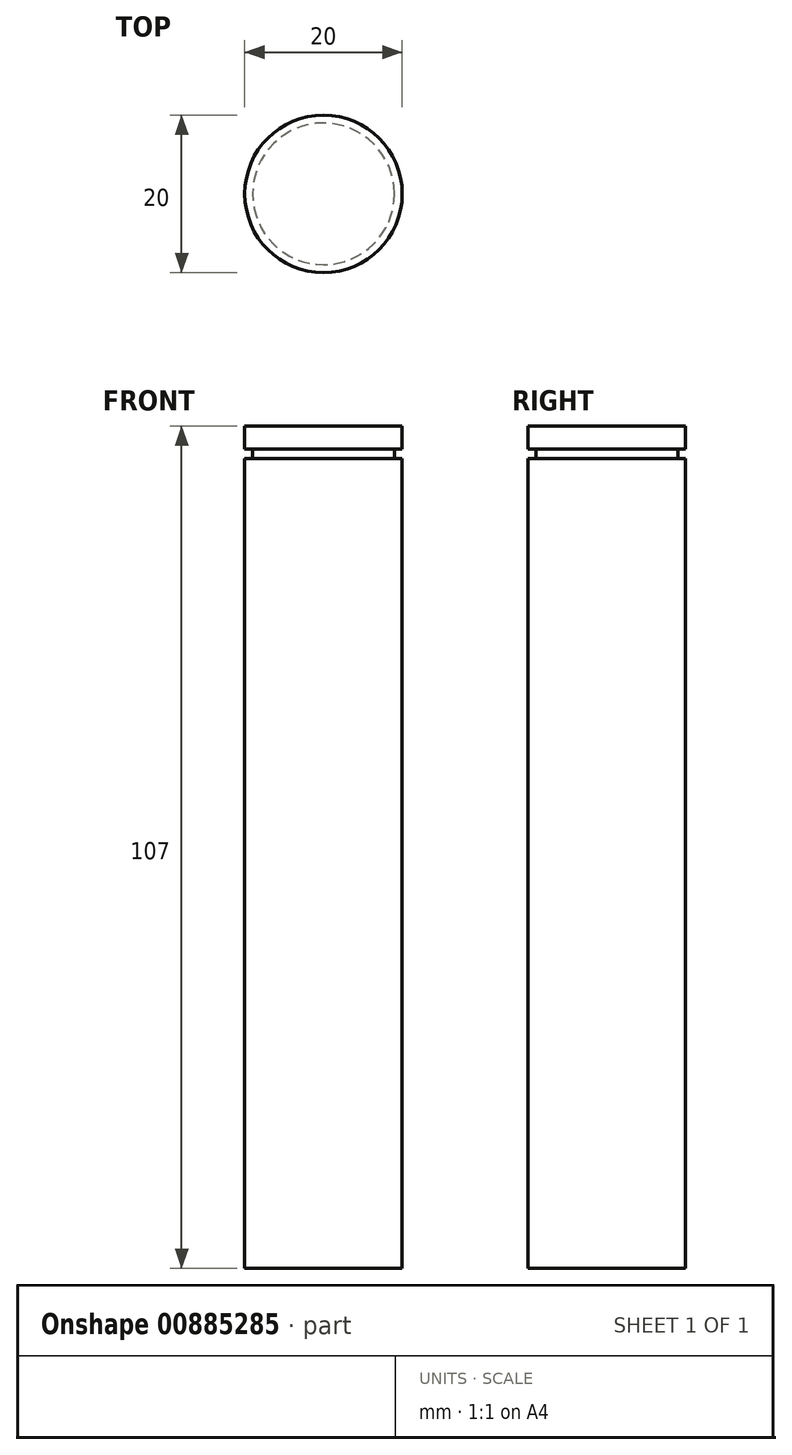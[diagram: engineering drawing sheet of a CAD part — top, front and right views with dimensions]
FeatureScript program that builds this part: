
annotation { "Feature Type Name" : "Feature", "Feature Type Description" : "" }
export const myFeature = defineFeature(function(context is Context, id is Id, definition is map)
    precondition{}
    {
        {
            var Q0;
            Q0=qCreatedBy(makeId("Front.planeOp"),FACE);
            var sketch = newSketch(context, id + "F0", { "sketchPlane" : qUnion([Q0])});
            skLineSegment(sketch, "E0.bottom", {"start": v(0, 0) * mm, "end": v(-20, 0) * mm});
            skLineSegment(sketch, "E0.top", {"start": v(0, 107) * mm, "end": v(-20, 107) * mm});
            skLineSegment(sketch, "E0.left", {"start": v(0, 0) * mm, "end": v(0, 107) * mm});
            skLineSegment(sketch, "E0.right", {"start": v(-20, 0) * mm, "end": v(-20, 107) * mm});
            skLineSegment(sketch, "E1", {"start": v(-10, 107) * mm, "end": v(-10, 0) * mm});
            skLineSegment(sketch, "E2.bottom", {"start": v(-20, 104.1) * mm, "end": v(-19, 104.1) * mm});
            skLineSegment(sketch, "E2.top", {"start": v(-20, 102.85) * mm, "end": v(-19, 102.85) * mm});
            skLineSegment(sketch, "E2.left", {"start": v(-20, 104.1) * mm, "end": v(-20, 102.85) * mm});
            skLineSegment(sketch, "E2.right", {"start": v(-19, 104.1) * mm, "end": v(-19, 102.85) * mm});
            skLineSegment(sketch, "E3.MirrorCS", {"start": v(-1, 104.1) * mm, "end": v(-1, 102.85) * mm});
            skLineSegment(sketch, "E4.MirrorCS", {"start": v(0, 104.1) * mm, "end": v(-1, 104.1) * mm});
            skLineSegment(sketch, "E5.MirrorCS", {"start": v(0, 102.85) * mm, "end": v(-1, 102.85) * mm});
            skSolve(sketch);
        }
        {
            var Q0;
            {var subQ0=sQuery(id+"F0.wireOp",EDGE,"E0.right");Q0=makeQuery(id+"F0.imprint","IMPRINT",FACE,{"disambiguationData":[TD([[makeQuery(id+"F0.imprint","IMPRINT",EDGE,{"derivedFrom":subQ0}),-1.0]])]});}
            var Q1;
            Q1=sQuery(id+"F0.wireOp",EDGE,"E1");
            revolve(context, id + "F1", {"surfaceOperationType" : NewSurfaceOperationType.NEW, "entities" : qUnion([Q0]), "axis" : qUnion([Q1]), "revolveType" : RevolveType.FULL});
        }
    });
